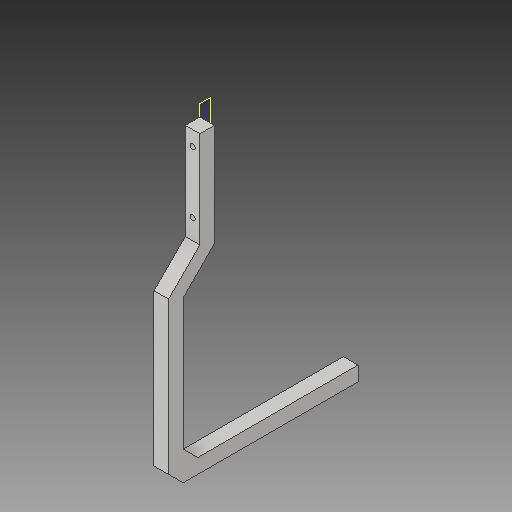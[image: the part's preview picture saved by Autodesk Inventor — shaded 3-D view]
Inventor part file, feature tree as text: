
AUTODESK INVENTOR PART (.ipt)
format: ipt  version: 2019.4 (Build 234330000, 330)  size: 114,688 bytes
history: native  units: mm
features: extrude x2, sketch x2, other x2, plane x1, chamfer x1, reference x1, projected_geometry x1
ambient origin geometry x8: Origin, YZ Plane, XZ Plane, XY Plane, X Axis, Y Axis, Z Axis, Center Point
bodies: Volumenkörper1 (feature_tree)
feature tree (10):
  plane  "Arbeitsebene1"
  extrude  "Extrusion1"  Depth=5.0mm
  extrude  "Extrusion2"  Depth=5.0mm
  chamfer  "Fase1"  Distance=5.0mm
  sketch  "Skizze1"  dims[d0=45.0deg d1=5.0mm]
  reference  "Referenz1"
  sketch  "Skizze2"  dims[d2=5.0mm d3=5.0mm d4=5.0mm d5=60.0mm d6=50.0mm d7=5.0mm d8=0.0mm d9=1.8mm d10=1.8mm d11=5.0mm d12=0.0mm d13=5.0mm d14=2.0mm d15=45.0deg]
  projected_geometry  "Projizierte Kontur1"
  other  "Full_HITscope_v0.iam"
  other  "05_Omniscope_base_v1:1"
